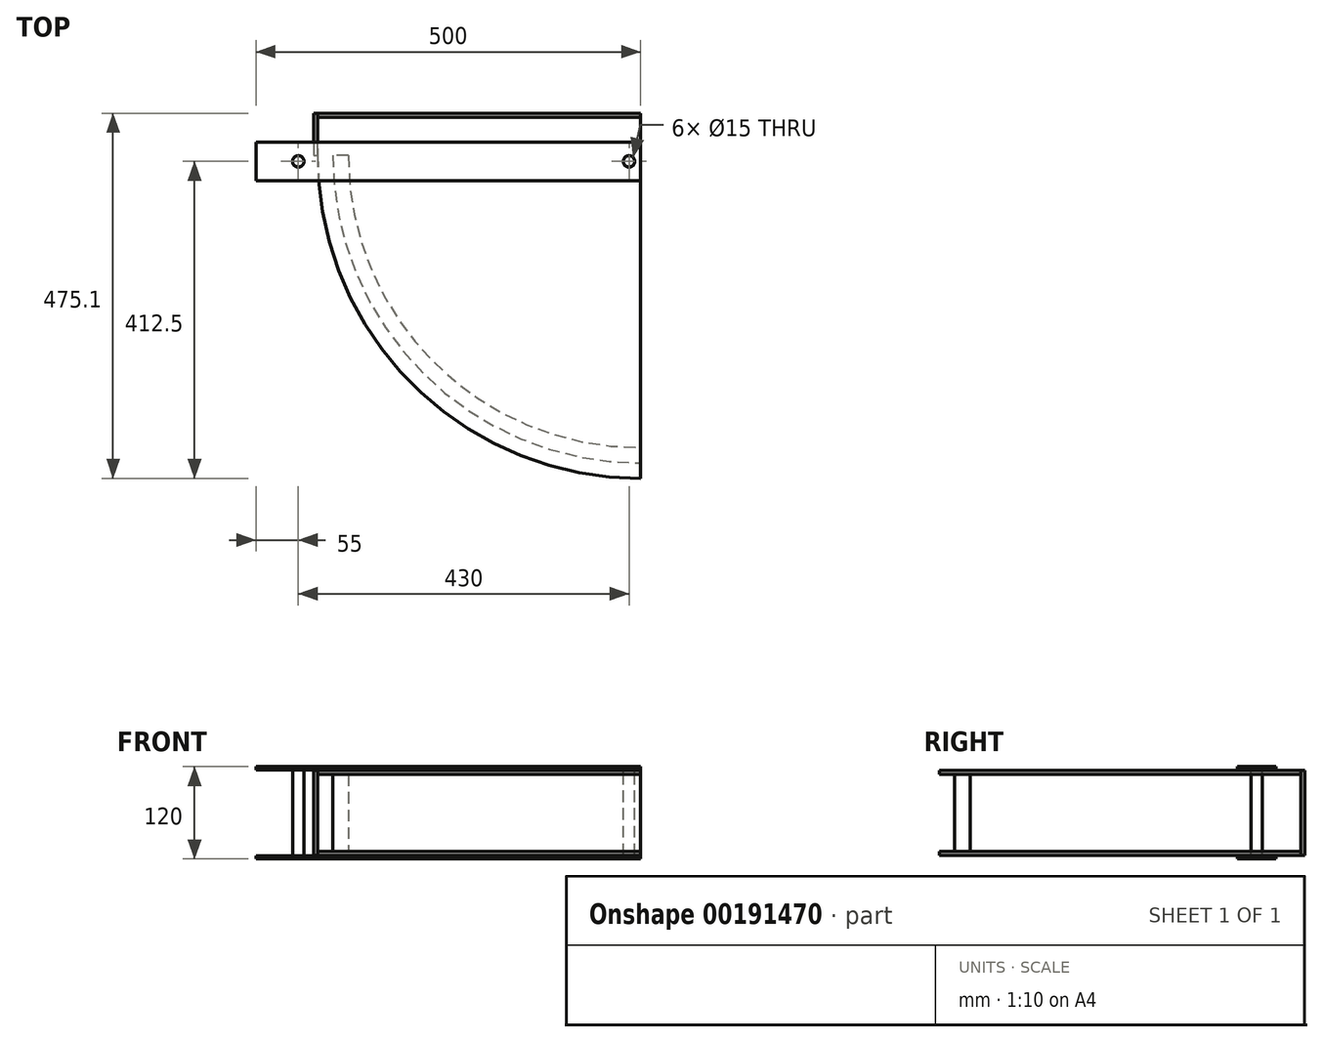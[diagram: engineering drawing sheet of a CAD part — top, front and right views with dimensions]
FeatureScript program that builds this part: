
annotation { "Feature Type Name" : "Feature", "Feature Type Description" : "" }
export const myFeature = defineFeature(function(context is Context, id is Id, definition is map)
    precondition{}
    {
        {
            var Q0;
            Q0=qCreatedBy(makeId("Top.planeOp"),FACE);
            var sketch = newSketch(context, id + "F0", { "sketchPlane" : qUnion([Q0])});
            skLineSegment(sketch, "E0", {"start": v(0, 0) * mm, "end": v(-400, 0) * mm});
            skArc(sketch, "E1", {"start": v(-400, 0) * mm, "mid": v(-282.84, -282.84) * mm, "end": v(0, -400) * mm});
            skLineSegment(sketch, "E2", {"start": v(0, 0) * mm, "end": v(0, -400) * mm});
            skArc(sketch, "E3.0", {"start": v(-380, 0) * mm, "mid": v(-268.7, -268.7) * mm, "end": v(0, -380) * mm});
            skLineSegment(sketch, "E4.bottom", {"start": v(-400, 0) * mm, "end": v(-380, 0) * mm});
            skLineSegment(sketch, "E4.top", {"start": v(-400, 50) * mm, "end": v(-380, 50) * mm});
            skLineSegment(sketch, "E4.left", {"start": v(-400, 0) * mm, "end": v(-400, 50) * mm});
            skLineSegment(sketch, "E4.right", {"start": v(-380, 0) * mm, "end": v(-380, 50) * mm});
            skSolve(sketch);
        }
        {
            var Q0;
            {var subQ0=sQuery(id+"F0.wireOp",EDGE,"E1");Q0=makeQuery(id+"F0.imprint","IMPRINT",FACE,{"disambiguationData":[TD([[makeQuery(id+"F0.imprint","IMPRINT",EDGE,{"derivedFrom":subQ0}),1.0]])]});}
            var Q1;
            Q1=makeQuery(id+"F0.imprint","IMPRINT",FACE,{"disambiguationData":[TD([[makeQuery(id+"F0.imprint","IMPRINT",EDGE,{"derivedFrom":sQuery(id+"F0.wireOp",EDGE,"E4.bottom")}),1.0]])]});
            extrude(context, id + "F1", {"entities" : qUnion([Q0, Q1]), "depth" : 100 * mm});
        }
        {
            var Q0;
            Q0=makeQuery(id+"F1.opExtrude","CAP_FACE",FACE,{"disambiguationData":[OSD([sQuery(id+"F0.wireOp",EDGE,"E0"),sQuery(id+"F0.wireOp",EDGE,"E1"),sQuery(id+"F0.wireOp",EDGE,"E2"),sQuery(id+"F0.wireOp",EDGE,"E3.0")])],"isStart":true});
            cPlane(context, id + "F2", {"entities" : qUnion([Q0]), "cplaneType" : CPlaneType.OFFSET, "offset" : 0 * mm, "width" : 150 * mm, "height" : 150 * mm});
        }
        {
            var Q0;
            Q0=qCreatedBy(id+"F2.planeOp",FACE);
            var sketch = newSketch(context, id + "F3", { "sketchPlane" : qUnion([Q0])});
            skLineSegment(sketch, "E5", {"start": v(0, 0) * mm, "end": v(0, 420) * mm});
            skLineSegment(sketch, "E6", {"start": v(0, 0) * mm, "end": v(-420, 0) * mm});
            skArc(sketch, "E7", {"start": v(0, 400) * mm, "mid": v(-282.84, 282.84) * mm, "end": v(-400, 0) * mm});
            skArc(sketch, "E8.0", {"start": v(0, 420) * mm, "mid": v(-296.98, 296.98) * mm, "end": v(-420, 0) * mm});
            skLineSegment(sketch, "E9.bottom", {"start": v(-420, 0) * mm, "end": v(0, 0) * mm});
            skLineSegment(sketch, "E9.top", {"start": v(-420, -50) * mm, "end": v(0, -50) * mm});
            skLineSegment(sketch, "E9.left", {"start": v(-420, 0) * mm, "end": v(-420, -50) * mm});
            skLineSegment(sketch, "E9.right", {"start": v(0, 0) * mm, "end": v(0, -50) * mm});
            skSolve(sketch);
        }
        {
            var Q0;
            Q0=qSketchRegion(id+"F3",true);
            extrude(context, id + "F4", {"entities" : qUnion([Q0]), "depth" : 5 * mm});
        }
        {
            var Q0;
            Q0=makeQuery(id+"F1.opExtrude","CAP_FACE",FACE,{"disambiguationData":[OSD([sQuery(id+"F0.wireOp",EDGE,"E0"),sQuery(id+"F0.wireOp",EDGE,"E1"),sQuery(id+"F0.wireOp",EDGE,"E2"),sQuery(id+"F0.wireOp",EDGE,"E3.0")])],"isStart":false});
            cPlane(context, id + "F5", {"entities" : qUnion([Q0]), "cplaneType" : CPlaneType.OFFSET, "offset" : 0 * mm, "width" : 150 * mm, "height" : 150 * mm});
        }
        {
            var Q0;
            Q0=qCreatedBy(id+"F5.planeOp",FACE);
            var sketch = newSketch(context, id + "F6", { "sketchPlane" : qUnion([Q0])});
            skLineSegment(sketch, "E10", {"start": v(0, 0) * mm, "end": v(0, -420) * mm});
            skLineSegment(sketch, "E11", {"start": v(0, 0) * mm, "end": v(-420, 0) * mm});
            skArc(sketch, "E12.0", {"start": v(-420, 0) * mm, "mid": v(-296.98, -296.98) * mm, "end": v(0, -420) * mm});
            skLineSegment(sketch, "E13.bottom", {"start": v(-420, 0) * mm, "end": v(0, 0) * mm});
            skLineSegment(sketch, "E13.top", {"start": v(-420, 50) * mm, "end": v(0, 50) * mm});
            skLineSegment(sketch, "E13.left", {"start": v(-420, 0) * mm, "end": v(-420, 50) * mm});
            skLineSegment(sketch, "E13.right", {"start": v(0, 0) * mm, "end": v(0, 50) * mm});
            skSolve(sketch);
        }
        {
            var Q0;
            Q0=qSketchRegion(id+"F6",true);
            extrude(context, id + "F7", {"entities" : qUnion([Q0]), "depth" : 5 * mm});
        }
        {
            var Q0;
            Q0=makeQuery(id+"F4.opExtrude","SWEPT_FACE",FACE,{"disambiguationData":[OSD([sQuery(id+"F3.wireOp",EDGE,"E9.top")])]});
            cPlane(context, id + "F8", {"entities" : qUnion([Q0]), "cplaneType" : CPlaneType.OFFSET, "offset" : 0 * mm, "width" : 150 * mm, "height" : 150 * mm});
        }
        {
            var Q0;
            Q0=qCreatedBy(id+"F8.planeOp",FACE);
            var sketch = newSketch(context, id + "F9", { "sketchPlane" : qUnion([Q0])});
            skLineSegment(sketch, "E14", {"start": v(0, -5) * mm, "end": v(0, 105) * mm});
            skLineSegment(sketch, "E15", {"start": v(0, -5) * mm, "end": v(420, -5) * mm});
            skLineSegment(sketch, "E16", {"start": v(420, -5) * mm, "end": v(420, 105) * mm});
            skLineSegment(sketch, "E17", {"start": v(420, 105) * mm, "end": v(0, 105) * mm});
            skSolve(sketch);
        }
        {
            var Q0;
            Q0=qSketchRegion(id+"F9",true);
            extrude(context, id + "F10", {"entities" : qUnion([Q0]), "depth" : 5.1 * mm});
        }
        {
            var Q0;
            Q0=makeQuery(id+"F7.opExtrude","CAP_FACE",FACE,{"disambiguationData":[OSD([sQuery(id+"F6.wireOp",EDGE,"E10"),sQuery(id+"F6.wireOp",EDGE,"E12.0"),sQuery(id+"F6.wireOp",EDGE,"E13.top"),sQuery(id+"F6.wireOp",EDGE,"E13.left"),sQuery(id+"F6.wireOp",EDGE,"E13.right")])],"isStart":false});
            var sketch = newSketch(context, id + "F11", { "sketchPlane" : qUnion([Q0])});
            skCircle(sketch, "E18", {"center": v(-15, -7.5) * mm, "radius": 7.5 * mm});
            skSolve(sketch);
        }
        {
            var Q0;
            Q0 = qSketchRegion(id + "F11", true);
            extrude(context, id + "F12", {"entities" : qUnion([Q0]), "operationType" : NewBodyOperationType.REMOVE, "endBound" : BoundingType.THROUGH_ALL, "oppositeDirection" : true, "depth" : 42 * mm});
        }
        {
            var Q0;
            Q0=makeQuery(id+"F7.opExtrude","CAP_FACE",FACE,{"disambiguationData":[OSD([sQuery(id+"F6.wireOp",EDGE,"E10"),sQuery(id+"F6.wireOp",EDGE,"E12.0"),sQuery(id+"F6.wireOp",EDGE,"E13.top"),sQuery(id+"F6.wireOp",EDGE,"E13.left"),sQuery(id+"F6.wireOp",EDGE,"E13.right")])],"isStart":false});
            cPlane(context, id + "F13", {"entities" : qUnion([Q0]), "cplaneType" : CPlaneType.OFFSET, "offset" : 5 * mm, "width" : 150 * mm, "height" : 150 * mm});
        }
        {
            var Q0;
            Q0=qCreatedBy(id+"F13.planeOp",FACE);
            var sketch = newSketch(context, id + "F14", { "sketchPlane" : qUnion([Q0])});
            skCircle(sketch, "E19", {"center": v(-15, -7.5) * mm, "radius": 7.25 * mm});
            skSolve(sketch);
        }
        {
            var Q0;
            Q0 = qSketchRegion(id + "F14", true);
            extrude(context, id + "F15", {"entities" : qUnion([Q0]), "oppositeDirection" : true, "depth" : 120 * mm});
        }
        {
            var Q0;
            Q0=makeQuery(id+"F15.opExtrude","CAP_FACE",FACE,{"disambiguationData":[OSD([sQuery(id+"F14.wireOp",EDGE,"E19")])],"isStart":true});
            cPlane(context, id + "F16", {"entities" : qUnion([Q0]), "cplaneType" : CPlaneType.OFFSET, "offset" : 0 * mm, "width" : 150 * mm, "height" : 150 * mm});
        }
        {
            var Q0;
            Q0=qCreatedBy(id+"F16.planeOp",FACE);
            var sketch = newSketch(context, id + "F17", { "sketchPlane" : qUnion([Q0])});
            skLineSegment(sketch, "E20.bottom", {"start": v(0, -32.5) * mm, "end": v(-500, -32.5) * mm});
            skLineSegment(sketch, "E20.top", {"start": v(0, 17.5) * mm, "end": v(-500, 17.5) * mm});
            skLineSegment(sketch, "E20.left", {"start": v(0, -32.5) * mm, "end": v(0, 17.5) * mm});
            skLineSegment(sketch, "E20.right", {"start": v(-500, -32.5) * mm, "end": v(-500, 17.5) * mm});
            skCircle(sketch, "E21", {"center": v(-15, -7.5) * mm, "radius": 7.5 * mm});
            skCircle(sketch, "E22", {"center": v(-445, -7.5) * mm, "radius": 7.5 * mm});
            skSolve(sketch);
        }
        {
            var Q0;
            Q0 = qSketchRegion(id + "F17", true);
            extrude(context, id + "F18", {"entities" : qUnion([Q0]), "operationType" : NewBodyOperationType.ADD, "oppositeDirection" : true, "depth" : 4 * mm});
        }
        {
            var Q0;
            Q0=qCreatedBy(id+"F5.planeOp",FACE);
            cPlane(context, id + "F19", {"entities" : qUnion([Q0]), "cplaneType" : CPlaneType.OFFSET, "offset" : 50 * mm, "oppositeDirection" : true, "width" : 150 * mm, "height" : 150 * mm});
        }
        {
            var Q0;
            Q0=makeQuery(id+"F18.opExtrude","SWEPT_BODY",BODY,{"disambiguationData":[OSD([sQuery(id+"F17.wireOp",EDGE,"E20.bottom"),sQuery(id+"F17.wireOp",EDGE,"E20.top"),sQuery(id+"F17.wireOp",EDGE,"E20.left"),sQuery(id+"F17.wireOp",EDGE,"E20.right"),sQuery(id+"F17.wireOp",EDGE,"E21")])]});
            var Q1;
            Q1=qCreatedBy(id+"F19.planeOp",FACE);
            mirror(context, id + "F20", {"entities" : qUnion([Q0]), "mirrorPlane" : qUnion([Q1])});
        }
        {
            var Q0;
            Q0=makeQuery(id+"F7.opExtrude","SWEPT_FACE",FACE,{"disambiguationData":[OSD([sQuery(id+"F6.wireOp",EDGE,"E10"),sQuery(id+"F6.wireOp",EDGE,"E13.right")])]});
            cPlane(context, id + "F21", {"entities" : qUnion([Q0]), "cplaneType" : CPlaneType.OFFSET, "offset" : (217.5 + 12.5) * mm, "oppositeDirection" : true, "width" : 150 * mm, "height" : 150 * mm});
        }
        {
            var Q0;
            Q0=makeQuery(id+"F15.opExtrude","SWEPT_BODY",BODY,{"disambiguationData":[OSD([sQuery(id+"F14.wireOp",EDGE,"E19")])]});
            var Q1;
            Q1=qCreatedBy(id+"F21.planeOp",FACE);
            mirror(context, id + "F22", {"entities" : qUnion([Q0]), "mirrorPlane" : qUnion([Q1])});
        }
        {
            var Q0;
            Q0=makeQuery(id+"F10.opExtrude","SWEPT_FACE",FACE,{"disambiguationData":[OSD([sQuery(id+"F9.wireOp",EDGE,"E16")])]});
            cPlane(context, id + "F23", {"entities" : qUnion([Q0]), "cplaneType" : CPlaneType.OFFSET, "offset" : 0 * mm, "width" : 150 * mm, "height" : 150 * mm});
        }
        {
            var Q0;
            Q0=qCreatedBy(id+"F23.planeOp",FACE);
            var sketch = newSketch(context, id + "F24", { "sketchPlane" : qUnion([Q0])});
            skLineSegment(sketch, "E23.bottom", {"start": v(-55, -5) * mm, "end": v(0, -5) * mm});
            skLineSegment(sketch, "E23.top", {"start": v(-55, 105) * mm, "end": v(0, 105) * mm});
            skLineSegment(sketch, "E23.left", {"start": v(-55, -5) * mm, "end": v(-55, 105) * mm});
            skLineSegment(sketch, "E23.right", {"start": v(0, -5) * mm, "end": v(0, 105) * mm});
            skSolve(sketch);
        }
        {
            var Q0;
            Q0 = qSketchRegion(id + "F24", true);
            extrude(context, id + "F25", {"entities" : qUnion([Q0]), "depth" : 5 * mm});
        }
    });
